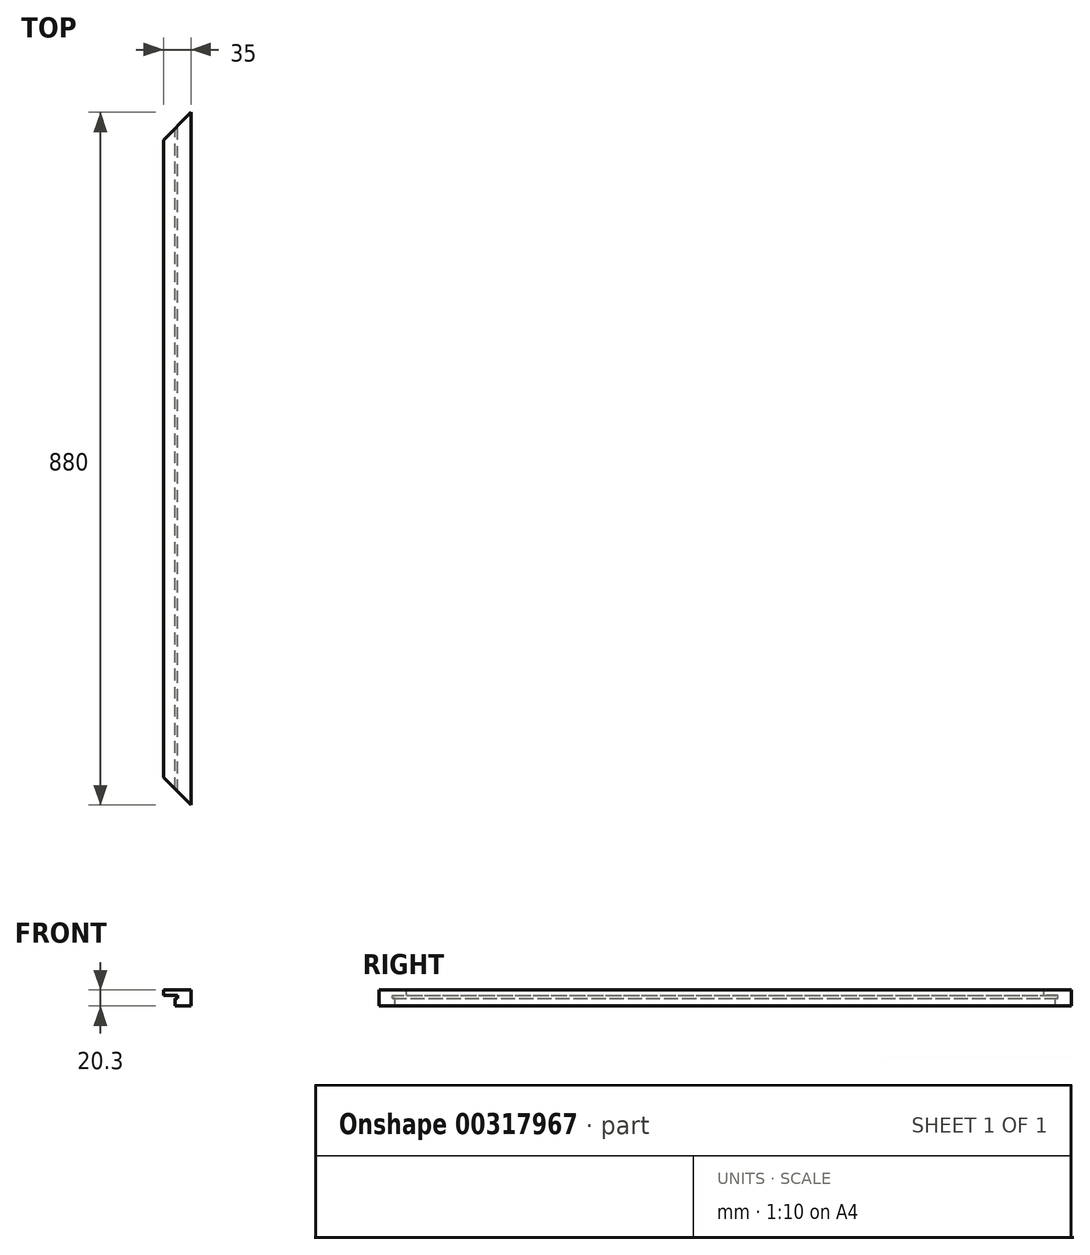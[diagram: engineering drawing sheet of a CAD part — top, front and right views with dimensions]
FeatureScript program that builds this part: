
annotation { "Feature Type Name" : "Feature", "Feature Type Description" : "" }
export const myFeature = defineFeature(function(context is Context, id is Id, definition is map)
    precondition{}
    {
        {
            var Q0;
            Q0=qCreatedBy(makeId("Front.planeOp"),FACE);
            var sketch = newSketch(context, id + "F0", { "sketchPlane" : qUnion([Q0])});
            skLineSegment(sketch, "E0", {"start": v(20.3, 20.3) * mm, "end": v(-14.7, 20.3) * mm});
            skLineSegment(sketch, "E1", {"start": v(-14.7, 20.3) * mm, "end": v(-14.7, 13.3) * mm});
            skLineSegment(sketch, "E2", {"start": v(-14.7, 13.3) * mm, "end": v(3, 13.3) * mm});
            skLineSegment(sketch, "E3", {"start": v(3, 13.3) * mm, "end": v(3, 10) * mm});
            skLineSegment(sketch, "E4", {"start": v(3, 10) * mm, "end": v(0, 10) * mm});
            skLineSegment(sketch, "E5", {"start": v(0, 10) * mm, "end": v(0, 0) * mm});
            skLineSegment(sketch, "E6", {"start": v(20.3, 20.3) * mm, "end": v(20.3, 0) * mm});
            skLineSegment(sketch, "E7", {"start": v(20.3, 0) * mm, "end": v(0, 0) * mm});
            skSolve(sketch);
        }
        {
            var Q0;
            Q0 = qSketchRegion(id + "F0", true);
            extrude(context, id + "F1", {"entities" : qUnion([Q0]), "endBound" : BoundingType.SYMMETRIC, "depth" : 880 * mm});
        }
        {
            var Q0;
            Q0=makeQuery(id+"F1.opExtrude","SWEPT_FACE",FACE,{"disambiguationData":[OSD([sQuery(id+"F0.wireOp",EDGE,"E0")])]});
            var sketch = newSketch(context, id + "F2", { "sketchPlane" : qUnion([Q0])});
            skLineSegment(sketch, "E8", {"start": v(20.3, 440) * mm, "end": v(-14.7, 405) * mm});
            skLineSegment(sketch, "E9", {"start": v(-14.7, 405) * mm, "end": v(-14.7, 440) * mm});
            skLineSegment(sketch, "E10", {"start": v(-14.7, 440) * mm, "end": v(20.3, 440) * mm});
            skLineSegment(sketch, "E11.MirrorCS", {"start": v(20.3, -440) * mm, "end": v(-14.7, -405) * mm});
            skLineSegment(sketch, "E12.MirrorCS", {"start": v(-14.7, -405) * mm, "end": v(-14.7, -440) * mm});
            skLineSegment(sketch, "E13.MirrorCS", {"start": v(-14.7, -440) * mm, "end": v(20.3, -440) * mm});
            skSolve(sketch);
        }
        {
            var Q0;
            Q0=makeQuery(id+"F2.imprint","IMPRINT",FACE,{"disambiguationData":[TD([[makeQuery(id+"F2.imprint","IMPRINT",EDGE,{"derivedFrom":sQuery(id+"F2.wireOp",EDGE,"E8")}),-1.0]])]});
            var Q1;
            Q1=makeQuery(id+"F2.imprint","IMPRINT",FACE,{"disambiguationData":[TD([[makeQuery(id+"F2.imprint","IMPRINT",EDGE,{"derivedFrom":sQuery(id+"F2.wireOp",EDGE,"E11.MirrorCS")}),1.0]])]});
            extrude(context, id + "F3", {"entities" : qUnion([Q0, Q1]), "operationType" : NewBodyOperationType.REMOVE, "oppositeDirection" : true, "depth" : 25.4 * mm});
        }
    });
